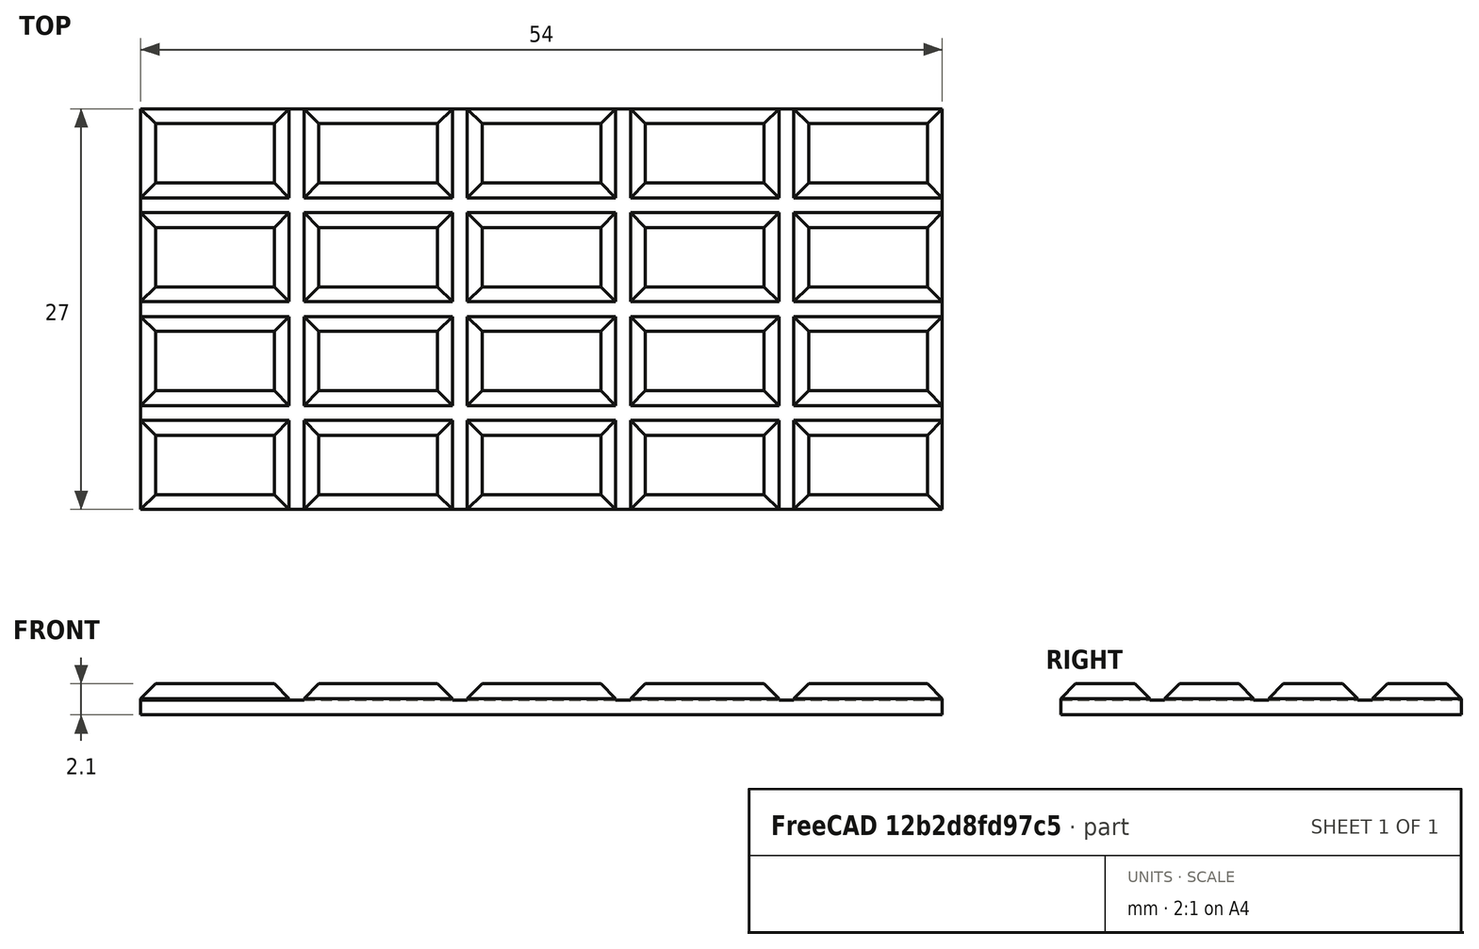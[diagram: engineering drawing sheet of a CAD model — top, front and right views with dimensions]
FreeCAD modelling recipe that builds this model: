
FCSTD DOCUMENT  (FreeCAD 1.0R39285 (Git))
Label: ojt1_t12r02_chocolat
License: All rights reserved
objects: Part::Box×2, Part::Chamfer×1, Part::FeaturePython×1, Part::MultiFuse×1
note: 4 computed .brp shape members not serialized (recipe doc carries the construction recipe); baked Part::Feature solids carry a one-line shape summary decoded from their .brp

FEATURE [Part::Box] Box  label="basis"
  AttacherType = Attacher::AttachEngine3D
  Height = 1
  Length = 54
  Width = 27
FEATURE [Part::Box] Box001  label="ounce"
  AttacherType = Attacher::AttachEngine3D
  Height = 1.1
  Length = 10
  Placement = pos=(0,0,1) rot=(0,0,1;0rad)
  Width = 6
FEATURE [Part::Chamfer] Chamfer
  Base = -> Box001
  EdgeLinks = -> Box001 [Edge2,Edge6,Edge10,Edge12]
  Edges = 4 edges r=1: [Edge2,Edge6,Edge10,Edge12]
FEATURE [Part::FeaturePython] Array  # Draft array (typed FeaturePython)
  AlwaysSyncPlacement = false
  Angle = 360
  ArrayType = 0
  Axis = (0,0,1)
  Base = -> Chamfer
  Center = (0,0,0)
  Count = 20
  ExpandArray = false
  Fuse = false
  IntervalAxis = (0,0,0)
  IntervalX = (11,0,0)
  IntervalY = (0,7,0)
  IntervalZ = (0,0,0)
  NumberCircles = 3
  NumberPolar = 5
  NumberX = 5
  NumberY = 4
  NumberZ = 1
  PlacementList = 20 placements: [(0,0,0),(0,7,0),(0,14,0),(0,21,0),(11,0,0),(11,7,0),(11,14,0),(11,21,0),(22,0,0),(22,7,0),(22,14,0),(22,21,0),(33,0,0),(33,7,0),(33,14,0),(33,21,0),(44,0,0),(44,7,0),(44,14,0),(44,21,0)]
  RadialDistance = 50
  ScaleList = (20) [(1,1,1),(1,1,1),(1,1,1),(1,1,1),(1,1,1),(1,1,1),(1,1,1),(1,1,1),(1,1,1),(1,1,1),(1,1,1),(1,1,1),(1,1,1),(1,1,1),(1,1,1),(1,1,1),(1,1,1),(1,1,1),(1,1,1),(1,1,1)]
  Symmetry = 1
  TangentialDistance = 25
FEATURE [Part::MultiFuse] Fusion  label="chocolat"
  Refine = true
  Shapes = -> [Box,Array]
